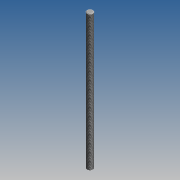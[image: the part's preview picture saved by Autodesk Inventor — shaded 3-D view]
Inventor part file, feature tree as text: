
AUTODESK INVENTOR PART (.ipt)
format: ipt  version: 2015 SP1 (Build 190203100, 203)  size: 180,224 bytes
history: native  units: mm
features: extrude x1, chamfer x1, thread x1, sketch x1
ambient origin geometry x8: Origin, YZ Plane, XZ Plane, XY Plane, X Axis, Y Axis, Z Axis, Center Point
bodies: Solid1 (feature_tree)
feature tree (4):
  extrude  "Extrusion1"  Depth=70.0mm TaperAngle=0.0deg
  chamfer  "Chamfer1"  Distance=0.3mm Angle=45.0deg
  thread  "Thread1"  [1 undecoded]
  sketch  "Sketch1"  dims[d0=3.0mm d1=70.0mm d2=0.0mm d3=0.3mm d4=2.0mm d5=45.0deg d6=10.0mm d7=0.0mm]
note: 1 required parameter value undecoded (feature->parameter linkage not recoverable at this tier; creation-order binding heuristic only, values carry confidence <= 0.55)
